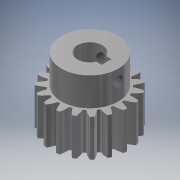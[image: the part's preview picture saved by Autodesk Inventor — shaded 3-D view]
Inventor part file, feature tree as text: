
AUTODESK INVENTOR PART (.ipt)
format: ipt  version: 2019 (Build 230136000, 136)  size: 303,616 bytes
history: native  units: mm (DEFAULTED — no unit token found)
features: sketch x7, extrude x6, plane x5, other x5
ambient origin geometry x8: Origin, YZ Plane, XZ Plane, XY Plane, X Axis, Y Axis, Z Axis, Center Point
bodies: Solid1 (feature_tree)
feature tree (23):
  extrude  "Extrusion1"  Depth=15.0mm TaperAngle=0.0deg
  plane  "Work Plane2"
  plane  "Work Plane8"
  plane  "Work Plane9"
  other  "正齒輪"
  extrude  "擠出2"  Depth=10.0mm TaperAngle=0.0deg
  extrude  "擠出3"  Depth=10.0mm
  extrude  "擠出4"  Depth=10.0mm TaperAngle=0.0deg
  plane  "工作平面11"
  extrude  "擠出5"  TaperAngle=0.0deg  [1 undecoded]
  plane  "工作平面12"
  extrude  "擠出6"  TaperAngle=0.0deg  [1 undecoded]
  other  "螺紋1"
  other  "螺紋2"
  sketch  "Sketch1"  dims[d0=31.5mm d1=15.0mm d2=0.0mm]
  sketch  "Sketch2"  dims[d3=28.5mm d4=10.0mm d5=0.0mm d16=57.0mm d17=0.0mm d34=1.65347mm d39=0.0mm d41=0.0mm d43=57.0mm d46=57.0mm d47=0.0mm d48=0.0mm d49=23.0mm d50=11.5mm d51=0.0mm d52=10.0mm d53=14.0mm d54=0.0mm d57=2.0mm d58=11.8mm d59=14.0mm d60=0.0mm d61=4.5mm d62=4.0mm d63=14.0mm d64=0.0mm d65=4.5mm d66=4.0mm d67=0.0mm d68=0.0mm d69=10.0mm d70=0.0mm d71=10.0mm d72=0.0mm]
  other  "Srf1"
  sketch  "草圖3"
  sketch  "草圖4"
  sketch  "草圖5"
  sketch  "草圖6"
  sketch  "草圖7"
  other  "節圓直徑"
note: 2 required parameter values undecoded (feature->parameter linkage not recoverable at this tier; creation-order binding heuristic only, values carry confidence <= 0.55)
